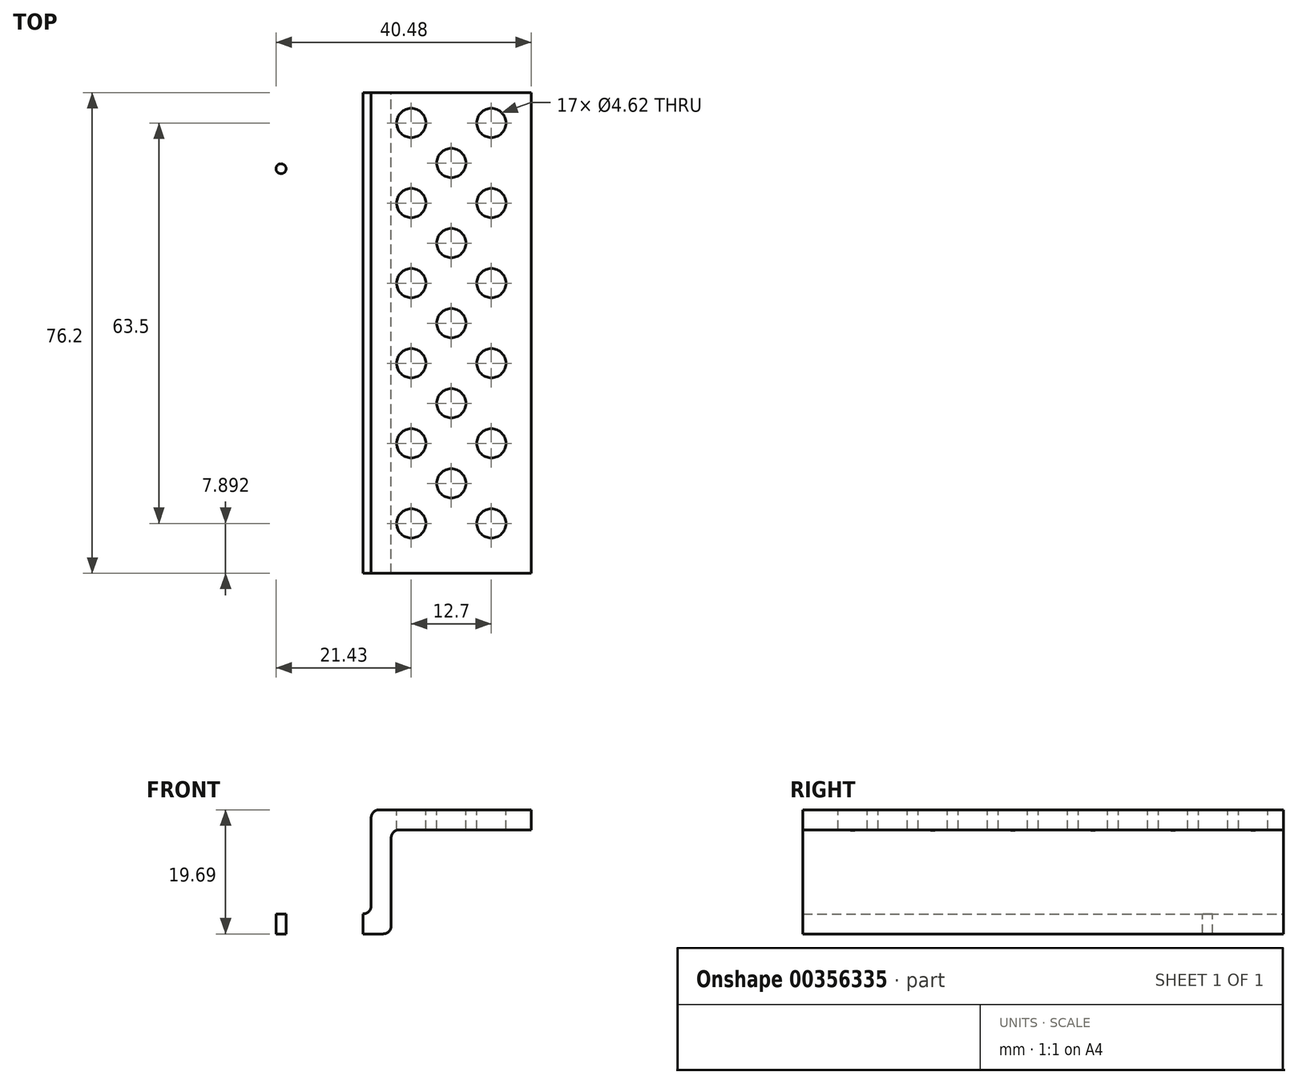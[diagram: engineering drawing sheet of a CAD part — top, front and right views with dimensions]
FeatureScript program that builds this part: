
annotation { "Feature Type Name" : "Feature", "Feature Type Description" : "" }
export const myFeature = defineFeature(function(context is Context, id is Id, definition is map)
    precondition{}
    {
        {
            var Q0;
            Q0=qCreatedBy(makeId("Front.planeOp"),FACE);
            var sketch = newSketch(context, id + "F0", { "sketchPlane" : qUnion([Q0])});
            skLineSegment(sketch, "E0.bottom", {"start": v(-53.86, 55.9) * mm, "end": v(-29.73, 55.9) * mm});
            skLineSegment(sketch, "E0.top", {"start": v(-50.69, 52.72) * mm, "end": v(-29.73, 52.72) * mm});
            skLineSegment(sketch, "E0.left", {"start": v(-55.13, 54.63) * mm, "end": v(-55.13, 52.72) * mm});
            skLineSegment(sketch, "E0.right", {"start": v(-29.73, 55.9) * mm, "end": v(-29.73, 52.72) * mm});
            skLineSegment(sketch, "E1.top", {"start": v(-55.13, 36.21) * mm, "end": v(-53.23, 36.21) * mm});
            skLineSegment(sketch, "E1.left", {"start": v(-55.13, 52.72) * mm, "end": v(-55.13, 40.66) * mm});
            skLineSegment(sketch, "E1.right", {"start": v(-51.96, 51.45) * mm, "end": v(-51.96, 37.48) * mm});
            skLineSegment(sketch, "E2.bottom", {"start": v(-55.13, 36.21) * mm, "end": v(-74.18, 36.21) * mm});
            skLineSegment(sketch, "E2.top", {"start": v(-56.4, 39.39) * mm, "end": v(-74.18, 39.39) * mm});
            skLineSegment(sketch, "E2.right", {"start": v(-74.18, 36.21) * mm, "end": v(-74.18, 39.39) * mm});
            skPoint(sketch, "E3.visualSharp", {"position": v(-55.13, 55.9) * mm});
            skArc(sketch, "E3.filletArc", {"start": v(-53.86, 55.9) * mm, "mid": v(-54.76, 55.52) * mm, "end": v(-55.13, 54.63) * mm});
            skArc(sketch, "E4.filletArc", {"start": v(-50.69, 52.72) * mm, "mid": v(-51.58, 52.35) * mm, "end": v(-51.96, 51.45) * mm});
            skPoint(sketch, "E5.visualSharp", {"position": v(-55.13, 39.39) * mm});
            skArc(sketch, "E5.filletArc", {"start": v(-56.4, 39.39) * mm, "mid": v(-55.5, 39.76) * mm, "end": v(-55.13, 40.66) * mm});
            skPoint(sketch, "E6.visualSharp", {"position": v(-51.96, 36.21) * mm});
            skArc(sketch, "E6.filletArc", {"start": v(-53.23, 36.21) * mm, "mid": v(-52.33, 36.58) * mm, "end": v(-51.96, 37.48) * mm});
            skSolve(sketch);
        }
        {
            var Q0;
            Q0 = qSketchRegion(id + "F0", true);
            extrude(context, id + "F1", {"entities" : qUnion([Q0]), "depth" : 76.2 * mm});
        }
        {
            var Q0;
            Q0=makeQuery(id+"F1.opExtrude","SWEPT_FACE",FACE,{"disambiguationData":[OSD([sQuery(id+"F0.wireOp",EDGE,"E2.top")])]});
            var sketch = newSketch(context, id + "F2", { "sketchPlane" : qUnion([Q0])});
            skLineSegment(sketch, "E7.bottom", {"start": v(-64.66, -21.59) * mm, "end": v(-71, -21.59) * mm});
            skLineSegment(sketch, "E7.top", {"start": v(-64.66, -54.61) * mm, "end": v(-71, -54.61) * mm});
            skLineSegment(sketch, "E7.left", {"start": v(-64.66, -21.59) * mm, "end": v(-64.66, -54.61) * mm});
            skLineSegment(sketch, "E7.right", {"start": v(-71, -21.59) * mm, "end": v(-71, -54.61) * mm});
            skCircle(sketch, "E8", {"center": v(-69.42, -64.14) * mm, "radius": 0.8 * mm});
            skPoint(sketch, "E9.startSnap0", {"position": v(-64.66, -38.1) * mm});
            skPoint(sketch, "E9.endSnap0", {"position": v(-74.18, -38.1) * mm});
            skCircle(sketch, "E10.MirrorC", {"center": v(-69.42, -12.07) * mm, "radius": 0.8 * mm});
            skSolve(sketch);
        }
        {
            var Q0;
            Q0=makeQuery(id+"F2.imprint","IMPRINT",FACE,{"disambiguationData":[TD([[makeQuery(id+"F2.imprint","IMPRINT",EDGE,{"derivedFrom":sQuery(id+"F2.wireOp",EDGE,"E8")}),1.0]])]});
            var Q1;
            Q1=makeQuery(id+"F2.imprint","IMPRINT",FACE,{"disambiguationData":[TD([[makeQuery(id+"F2.imprint","IMPRINT",EDGE,{"derivedFrom":sQuery(id+"F2.wireOp",EDGE,"E7.bottom")}),1.0]])]});
            var Q2;
            Q2=makeQuery(id+"F2.imprint","IMPRINT",FACE,{"disambiguationData":[TD([[makeQuery(id+"F2.imprint","IMPRINT",EDGE,{"derivedFrom":sQuery(id+"F2.wireOp",EDGE,"E10.MirrorC")}),-1.0]])]});
            extrude(context, id + "F3", {"entities" : qUnion([Q0, Q1, Q2]), "operationType" : NewBodyOperationType.REMOVE, "oppositeDirection" : true, "depth" : 5.84 * mm});
        }
        {
            var Q0;
            Q0=makeQuery(id+"F1.opExtrude","SWEPT_FACE",FACE,{"disambiguationData":[OSD([sQuery(id+"F0.wireOp",EDGE,"E0.bottom")])]});
            var sketch = newSketch(context, id + "F4", { "sketchPlane" : qUnion([Q0])});
            skCircle(sketch, "E11", {"center": v(-48.78, -4.8) * mm, "radius": 2.31 * mm});
            skCircle(sketch, "E12.1.0.0", {"center": v(-48.78, -17.5) * mm, "radius": 2.31 * mm});
            skCircle(sketch, "E12.2.0.0", {"center": v(-48.78, -30.2) * mm, "radius": 2.31 * mm});
            skCircle(sketch, "E12.3.0.0", {"center": v(-48.78, -42.9) * mm, "radius": 2.31 * mm});
            skLineSegment(sketch, "E12.direction1", {"start": v(-48.78, -4.8) * mm, "end": v(-48.78, -17.5) * mm, "construction": true});
            skCircle(sketch, "E13", {"center": v(-42.43, -11.16) * mm, "radius": 2.31 * mm});
            skPoint(sketch, "E13.centerSnap0", {"position": v(-48.78, -11.16) * mm});
            skCircle(sketch, "E14.1.0.0", {"center": v(-42.43, -23.86) * mm, "radius": 2.31 * mm});
            skCircle(sketch, "E14.2.0.0", {"center": v(-42.43, -36.56) * mm, "radius": 2.31 * mm});
            skLineSegment(sketch, "E14.direction1", {"start": v(-42.43, -11.16) * mm, "end": v(-42.43, -23.86) * mm, "construction": true});
            skCircle(sketch, "E15", {"center": v(-36.08, -4.8) * mm, "radius": 2.31 * mm});
            skCircle(sketch, "E16.1.0.0", {"center": v(-36.08, -17.5) * mm, "radius": 2.31 * mm});
            skCircle(sketch, "E16.2.0.0", {"center": v(-36.08, -30.2) * mm, "radius": 2.31 * mm});
            skCircle(sketch, "E16.3.0.0", {"center": v(-36.08, -42.9) * mm, "radius": 2.31 * mm});
            skLineSegment(sketch, "E16.direction1", {"start": v(-36.08, -4.8) * mm, "end": v(-36.08, -17.5) * mm, "construction": true});
            skCircle(sketch, "E17.0.1.0", {"center": v(-36.08, -55.6) * mm, "radius": 2.31 * mm});
            skCircle(sketch, "E17.0.2.0", {"center": v(-36.08, -68.3) * mm, "radius": 2.31 * mm});
            skLineSegment(sketch, "E17.direction1", {"start": v(-36.08, -42.9) * mm, "end": v(-10.68, -42.9) * mm, "construction": true});
            skLineSegment(sketch, "E17.direction2", {"start": v(-36.08, -42.9) * mm, "end": v(-36.08, -55.6) * mm, "construction": true});
            skCircle(sketch, "E18.0.1.0", {"center": v(-42.43, -49.26) * mm, "radius": 2.31 * mm});
            skCircle(sketch, "E18.0.2.0", {"center": v(-42.43, -61.96) * mm, "radius": 2.31 * mm});
            skLineSegment(sketch, "E18.direction1", {"start": v(-42.43, -36.56) * mm, "end": v(-33.55, -36.63) * mm, "construction": true});
            skLineSegment(sketch, "E18.direction2", {"start": v(-42.43, -36.56) * mm, "end": v(-42.43, -49.26) * mm, "construction": true});
            skCircle(sketch, "E19.0.1.0", {"center": v(-48.78, -55.6) * mm, "radius": 2.31 * mm});
            skCircle(sketch, "E19.0.2.0", {"center": v(-48.78, -68.3) * mm, "radius": 2.31 * mm});
            skLineSegment(sketch, "E19.direction1", {"start": v(-48.78, -42.9) * mm, "end": v(-42.94, -42.9) * mm, "construction": true});
            skLineSegment(sketch, "E19.direction2", {"start": v(-48.78, -42.9) * mm, "end": v(-48.78, -55.6) * mm, "construction": true});
            skSolve(sketch);
        }
        {
            var Q0;
            Q0=makeQuery(id+"F4.imprint","IMPRINT",FACE,{"disambiguationData":[TD([[makeQuery(id+"F4.imprint","IMPRINT",EDGE,{"derivedFrom":sQuery(id+"F4.wireOp",EDGE,"E19.0.1.0")}),1.0]])]});
            var Q1;
            Q1=makeQuery(id+"F4.imprint","IMPRINT",FACE,{"disambiguationData":[TD([[makeQuery(id+"F4.imprint","IMPRINT",EDGE,{"derivedFrom":sQuery(id+"F4.wireOp",EDGE,"E19.0.2.0")}),1.0]])]});
            var Q2;
            Q2=makeQuery(id+"F4.imprint","IMPRINT",FACE,{"disambiguationData":[TD([[makeQuery(id+"F4.imprint","IMPRINT",EDGE,{"derivedFrom":sQuery(id+"F4.wireOp",EDGE,"E18.0.2.0")}),1.0]])]});
            var Q3;
            Q3=makeQuery(id+"F4.imprint","IMPRINT",FACE,{"disambiguationData":[TD([[makeQuery(id+"F4.imprint","IMPRINT",EDGE,{"derivedFrom":sQuery(id+"F4.wireOp",EDGE,"E17.0.2.0")}),1.0]])]});
            var Q4;
            Q4=makeQuery(id+"F4.imprint","IMPRINT",FACE,{"disambiguationData":[TD([[makeQuery(id+"F4.imprint","IMPRINT",EDGE,{"derivedFrom":sQuery(id+"F4.wireOp",EDGE,"E17.0.1.0")}),1.0]])]});
            var Q5;
            Q5=makeQuery(id+"F4.imprint","IMPRINT",FACE,{"disambiguationData":[TD([[makeQuery(id+"F4.imprint","IMPRINT",EDGE,{"derivedFrom":sQuery(id+"F4.wireOp",EDGE,"E16.3.0.0")}),1.0]])]});
            var Q6;
            Q6=makeQuery(id+"F4.imprint","IMPRINT",FACE,{"disambiguationData":[TD([[makeQuery(id+"F4.imprint","IMPRINT",EDGE,{"derivedFrom":sQuery(id+"F4.wireOp",EDGE,"E18.0.1.0")}),1.0]])]});
            var Q7;
            Q7=makeQuery(id+"F4.imprint","IMPRINT",FACE,{"disambiguationData":[TD([[makeQuery(id+"F4.imprint","IMPRINT",EDGE,{"derivedFrom":sQuery(id+"F4.wireOp",EDGE,"E12.3.0.0")}),1.0]])]});
            var Q8;
            Q8=makeQuery(id+"F4.imprint","IMPRINT",FACE,{"disambiguationData":[TD([[makeQuery(id+"F4.imprint","IMPRINT",EDGE,{"derivedFrom":sQuery(id+"F4.wireOp",EDGE,"E14.2.0.0")}),1.0]])]});
            var Q9;
            Q9=makeQuery(id+"F4.imprint","IMPRINT",FACE,{"disambiguationData":[TD([[makeQuery(id+"F4.imprint","IMPRINT",EDGE,{"derivedFrom":sQuery(id+"F4.wireOp",EDGE,"E16.2.0.0")}),1.0]])]});
            var Q10;
            Q10=makeQuery(id+"F4.imprint","IMPRINT",FACE,{"disambiguationData":[TD([[makeQuery(id+"F4.imprint","IMPRINT",EDGE,{"derivedFrom":sQuery(id+"F4.wireOp",EDGE,"E12.2.0.0")}),1.0]])]});
            var Q11;
            Q11=makeQuery(id+"F4.imprint","IMPRINT",FACE,{"disambiguationData":[TD([[makeQuery(id+"F4.imprint","IMPRINT",EDGE,{"derivedFrom":sQuery(id+"F4.wireOp",EDGE,"E14.1.0.0")}),1.0]])]});
            var Q12;
            Q12=makeQuery(id+"F4.imprint","IMPRINT",FACE,{"disambiguationData":[TD([[makeQuery(id+"F4.imprint","IMPRINT",EDGE,{"derivedFrom":sQuery(id+"F4.wireOp",EDGE,"E16.1.0.0")}),1.0]])]});
            var Q13;
            Q13=makeQuery(id+"F4.imprint","IMPRINT",FACE,{"disambiguationData":[TD([[makeQuery(id+"F4.imprint","IMPRINT",EDGE,{"derivedFrom":sQuery(id+"F4.wireOp",EDGE,"E13")}),1.0]])]});
            var Q14;
            Q14=makeQuery(id+"F4.imprint","IMPRINT",FACE,{"disambiguationData":[TD([[makeQuery(id+"F4.imprint","IMPRINT",EDGE,{"derivedFrom":sQuery(id+"F4.wireOp",EDGE,"E12.1.0.0")}),1.0]])]});
            var Q15;
            Q15=makeQuery(id+"F4.imprint","IMPRINT",FACE,{"disambiguationData":[TD([[makeQuery(id+"F4.imprint","IMPRINT",EDGE,{"derivedFrom":sQuery(id+"F4.wireOp",EDGE,"E15")}),1.0]])]});
            var Q16;
            Q16=makeQuery(id+"F4.imprint","IMPRINT",FACE,{"disambiguationData":[TD([[makeQuery(id+"F4.imprint","IMPRINT",EDGE,{"derivedFrom":sQuery(id+"F4.wireOp",EDGE,"E11")}),1.0]])]});
            extrude(context, id + "F5", {"entities" : qUnion([Q0, Q1, Q2, Q3, Q4, Q5, Q6, Q7, Q8, Q9, Q10, Q11, Q12, Q13, Q14, Q15, Q16]), "operationType" : NewBodyOperationType.REMOVE, "oppositeDirection" : true, "depth" : 3.8 * mm});
        }
    });
